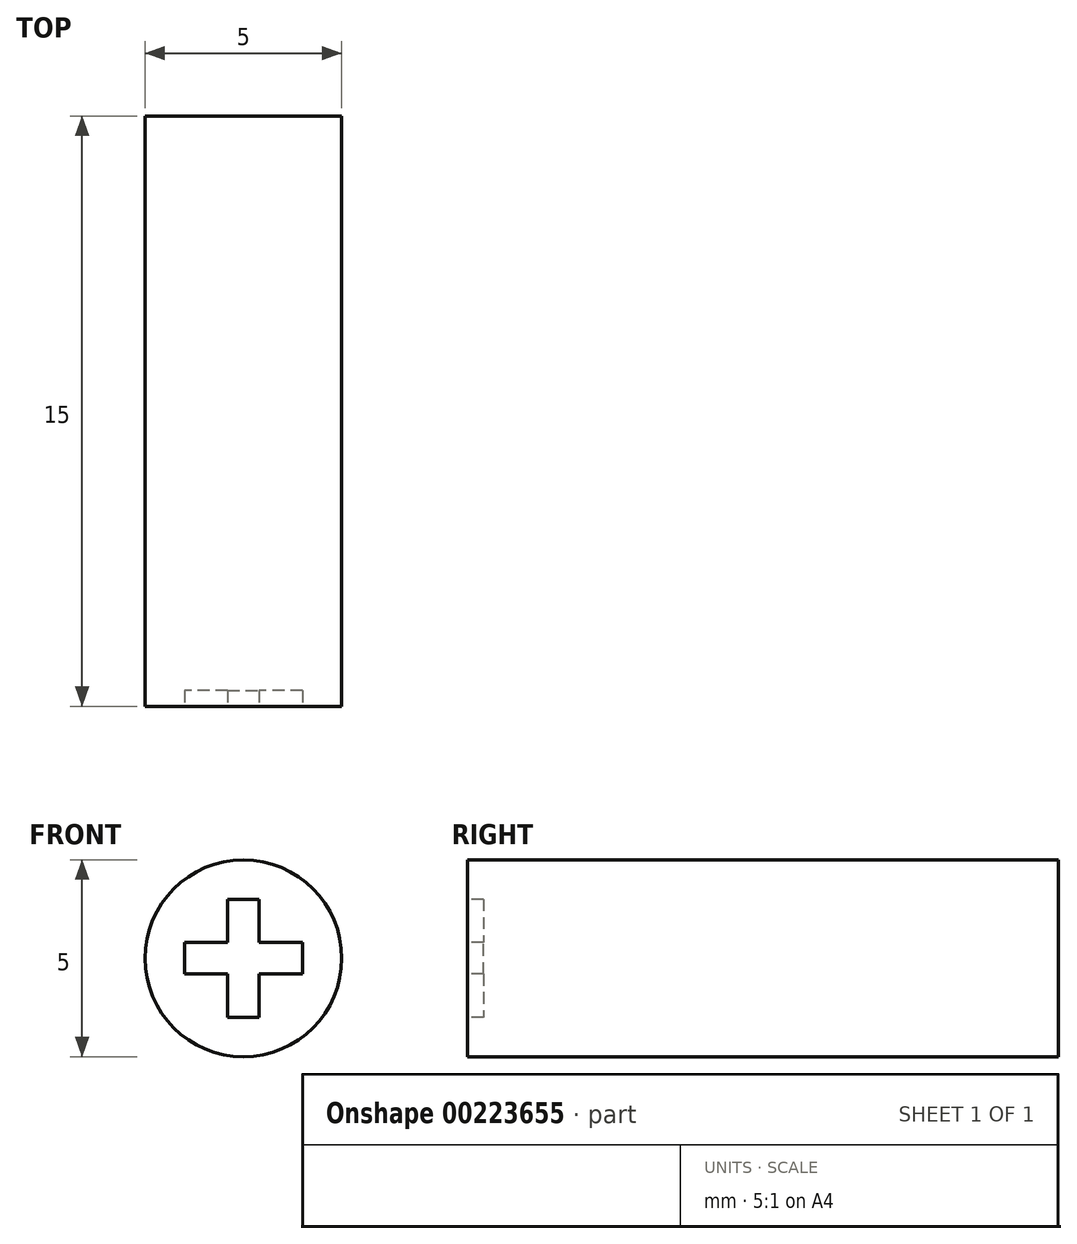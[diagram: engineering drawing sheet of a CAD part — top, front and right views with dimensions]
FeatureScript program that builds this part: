
annotation { "Feature Type Name" : "Feature", "Feature Type Description" : "" }
export const myFeature = defineFeature(function(context is Context, id is Id, definition is map)
    precondition{}
    {
        {
            var Q0;
            Q0=qCreatedBy(makeId("Top.planeOp"),FACE);
            var sketch = newSketch(context, id + "F0", { "sketchPlane" : qUnion([Q0])});
            skLineSegment(sketch, "E0", {"start": v(-93.68, 0) * mm, "end": v(54.32, 0) * mm});
            skLineSegment(sketch, "E1", {"start": v(54.32, 0) * mm, "end": v(54.32, -12) * mm});
            skLineSegment(sketch, "E2", {"start": v(54.32, -12) * mm, "end": v(-93.68, -12) * mm});
            skLineSegment(sketch, "E3", {"start": v(-93.68, -12) * mm, "end": v(-93.68, 0) * mm});
            skLineSegment(sketch, "E4", {"start": v(-79.68, 0) * mm, "end": v(-79.68, -4) * mm});
            skLineSegment(sketch, "E5", {"start": v(-79.68, -4) * mm, "end": v(-79.68, -8) * mm});
            skLineSegment(sketch, "E6", {"start": v(-79.68, -8) * mm, "end": v(-79.68, -12) * mm});
            skLineSegment(sketch, "E7", {"start": v(40.32, 0) * mm, "end": v(40.32, -4) * mm});
            skLineSegment(sketch, "E8", {"start": v(40.32, -4) * mm, "end": v(40.32, -8) * mm});
            skLineSegment(sketch, "E9", {"start": v(40.32, -8) * mm, "end": v(40.32, -12) * mm});
            skLineSegment(sketch, "E10", {"start": v(-79.68, -4) * mm, "end": v(40.32, -4) * mm});
            skLineSegment(sketch, "E11", {"start": v(40.32, -8) * mm, "end": v(-79.68, -8) * mm});
            skSolve(sketch);
        }
        {
            var Q0;
            Q0 = qSketchRegion(id + "F0", true);
            extrude(context, id + "F1", {"entities" : qUnion([Q0]), "depth" : 4 * mm});
        }
        {
            var Q0;
            Q0=makeQuery(id+"F1.opExtrude","SWEPT_BODY",BODY,{"disambiguationData":[OSD([sQuery(id+"F0.wireOp",EDGE,"E0"),sQuery(id+"F0.wireOp",EDGE,"E1"),sQuery(id+"F0.wireOp",EDGE,"E2"),sQuery(id+"F0.wireOp",EDGE,"E3"),sQuery(id+"F0.wireOp",EDGE,"E5"),sQuery(id+"F0.wireOp",EDGE,"E8"),sQuery(id+"F0.wireOp",EDGE,"E10"),sQuery(id+"F0.wireOp",EDGE,"E11")])]});
            deleteBodies(context, id + "F2", {"entities" : qUnion([Q0])});
        }
        {
            var Q0;
            Q0=qCreatedBy(makeId("Front.planeOp"),FACE);
            var sketch = newSketch(context, id + "F3", { "sketchPlane" : qUnion([Q0])});
            skCircle(sketch, "E12", {"center": v(0, 0) * mm, "radius": 2.5 * mm});
            skSolve(sketch);
        }
        {
            var Q0;
            Q0 = qSketchRegion(id + "F3", true);
            extrude(context, id + "F4", {"entities" : qUnion([Q0]), "depth" : 15 * mm});
        }
        {
            var Q0;
            Q0=makeQuery(id+"F4.opExtrude","CAP_FACE",FACE,{"disambiguationData":[OSD([sQuery(id+"F3.wireOp",EDGE,"E12")])],"isStart":false});
            var sketch = newSketch(context, id + "F5", { "sketchPlane" : qUnion([Q0])});
            skLineSegment(sketch, "E13", {"start": v(0, 0) * mm, "end": v(0, 1.5) * mm});
            skLineSegment(sketch, "E14", {"start": v(0, 0) * mm, "end": v(0, -1.5) * mm});
            skLineSegment(sketch, "E15", {"start": v(0, 0) * mm, "end": v(-1.5, 0) * mm});
            skLineSegment(sketch, "E16", {"start": v(0, 0) * mm, "end": v(1.5, 0) * mm});
            skLineSegment(sketch, "E17", {"start": v(0, 1.5) * mm, "end": v(-0.4, 1.5) * mm});
            skLineSegment(sketch, "E18", {"start": v(0, 1.5) * mm, "end": v(0.4, 1.5) * mm});
            skLineSegment(sketch, "E19", {"start": v(1.5, 0) * mm, "end": v(1.5, 0.4) * mm});
            skLineSegment(sketch, "E20", {"start": v(1.5, 0) * mm, "end": v(1.5, -0.4) * mm});
            skLineSegment(sketch, "E21", {"start": v(-0.4, 1.5) * mm, "end": v(-0.4, -1.5) * mm});
            skLineSegment(sketch, "E22", {"start": v(-0.4, -1.5) * mm, "end": v(0, -1.5) * mm});
            skLineSegment(sketch, "E23", {"start": v(0.4, 1.5) * mm, "end": v(0.4, -1.5) * mm});
            skLineSegment(sketch, "E24", {"start": v(0, -1.5) * mm, "end": v(0.4, -1.5) * mm});
            skLineSegment(sketch, "E25", {"start": v(1.5, 0.4) * mm, "end": v(-1.5, 0.4) * mm});
            skLineSegment(sketch, "E26", {"start": v(-1.5, 0.4) * mm, "end": v(-1.5, 0) * mm});
            skLineSegment(sketch, "E27", {"start": v(1.5, -0.4) * mm, "end": v(-1.5, -0.4) * mm});
            skLineSegment(sketch, "E28", {"start": v(-1.5, -0.4) * mm, "end": v(-1.5, 0) * mm});
            skSolve(sketch);
        }
        {
            var Q0;
            Q0 = qSketchRegion(id + "F5", true);
            extrude(context, id + "F6", {"entities" : qUnion([Q0]), "operationType" : NewBodyOperationType.REMOVE, "oppositeDirection" : true, "depth" : 0.4 * mm});
        }
    });
